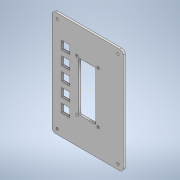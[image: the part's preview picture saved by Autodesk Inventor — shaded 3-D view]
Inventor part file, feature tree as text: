
AUTODESK INVENTOR PART (.ipt)
format: ipt  version: 2021 (Build 250183000, 183)  size: 220,160 bytes
history: native  units: mm
features: reference x32, sketch x7, extrude x6, other x3, pattern_linear x1
ambient origin geometry x8: Origin, YZ Plane, XZ Plane, XY Plane, X Axis, Y Axis, Z Axis, Center Point
bodies: Body1 (feature_tree)
feature tree (49):
  extrude  "Extrusion2"  Depth=3.0mm
  extrude  "Extrusion3"  Depth=2.0mm TaperAngle=0.0deg
  extrude  "Extrusion4"  Depth=2.0mm
  extrude  "Extrusion5"  Depth=0.2mm
  extrude  "Extrusion6"  Depth=0.2mm
  pattern_linear  "Rectangular Pattern1"  Spacing1=12.2mm  [1 undecoded]
  extrude  "Extrusion9"  Depth=20.0mm
  sketch  "Sketch10"  dims[d17=12.2mm d18=12.2mm d19=20.0mm d21=2.0mm d22=0.0mm d23=30.0mm d25=20.0mm d26=30.0mm d28=20.0mm d38=4.0mm d40=4.0mm d41=2.0mm d42=5.0mm d43=4.0mm d44=0.0mm]
  sketch  "Sketch2"  dims[d2=3.0mm d3=0.0mm d4=0.2mm]
  reference  "Reference9"
  reference  "Reference10"
  reference  "Reference11"
  reference  "Reference12"
  reference  "Reference13"
  reference  "Reference14"
  reference  "Reference15"
  reference  "Reference16"
  reference  "Reference17"
  reference  "Reference18"
  reference  "Reference19"
  reference  "Reference20"
  sketch  "Sketch3"  dims[d5=2.0mm d6=2.0mm d7=0.0mm]
  reference  "Reference21"
  reference  "Reference22"
  reference  "Reference23"
  reference  "Reference24"
  reference  "Reference25"
  reference  "Reference26"
  reference  "Reference27"
  reference  "Reference28"
  sketch  "Sketch4"  dims[d8=2.0mm d9=0.0mm d10=0.3mm]
  reference  "Reference29"
  reference  "Reference30"
  reference  "Reference31"
  reference  "Reference32"
  reference  "Reference33"
  reference  "Reference34"
  reference  "Reference35"
  reference  "Reference36"
  sketch  "Sketch5"  dims[d11=0.2mm d12=0.2mm]
  reference  "Reference37"
  reference  "Reference38"
  reference  "Reference39"
  reference  "Reference40"
  sketch  "Sketch6"  dims[d13=0.2mm d14=0.2mm]
  sketch  "Sketch9"  dims[d15=2.0mm d16=0.0mm]
  other  "Chestbox_with_electronical_devices.iam"
  other  "chestbox:1"
  other  "STEP 1602 Serial LCD Module:1"
note: 1 required parameter value undecoded (feature->parameter linkage not recoverable at this tier; creation-order binding heuristic only, values carry confidence <= 0.55)
